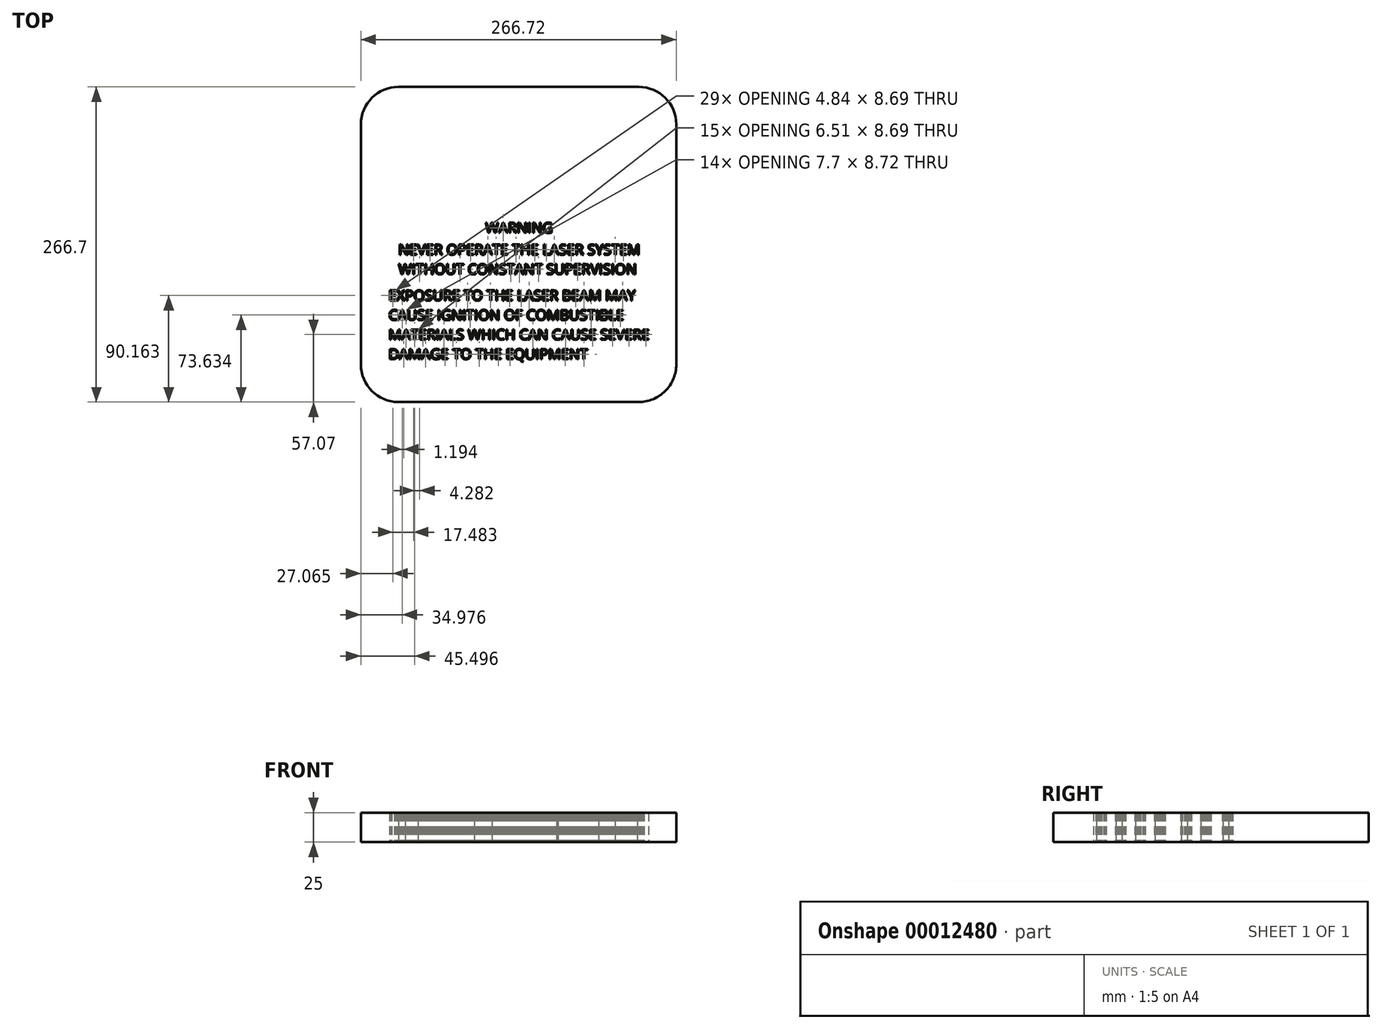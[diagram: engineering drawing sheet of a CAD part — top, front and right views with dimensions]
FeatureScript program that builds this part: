
annotation { "Feature Type Name" : "Feature", "Feature Type Description" : "" }
export const myFeature = defineFeature(function(context is Context, id is Id, definition is map)
    precondition{}
    {
        {
            var Q0;
            Q0=qCreatedBy(makeId("Top.planeOp"),FACE);
            var sketch = newSketch(context, id + "F0", { "sketchPlane" : qUnion([Q0])});
            skLineSegment(sketch, "E0.rect.top", {"start": v(101.61, 127) * mm, "end": v(-101.61, 127) * mm});
            skLineSegment(sketch, "E0.rect.left", {"start": v(127.01, -101.6) * mm, "end": v(127.01, 101.6) * mm});
            skLineSegment(sketch, "E0.rect.right", {"start": v(-127.01, -101.6) * mm, "end": v(-127.01, 101.6) * mm});
            skPoint(sketch, "E1.visualSharp", {"position": v(-127.01, 127) * mm});
            skArc(sketch, "E1.filletArc", {"start": v(-101.61, 127) * mm, "mid": v(-119.57, 119.56) * mm, "end": v(-127.01, 101.6) * mm});
            skPoint(sketch, "E2.visualSharp", {"position": v(127.01, 127) * mm});
            skArc(sketch, "E2.filletArc", {"start": v(127.01, 101.6) * mm, "mid": v(119.57, 119.56) * mm, "end": v(101.61, 127) * mm});
            skPoint(sketch, "E3.visualSharp", {"position": v(127.01, -127) * mm});
            skArc(sketch, "E3.filletArc", {"start": v(101.61, -127) * mm, "mid": v(119.57, -119.56) * mm, "end": v(127.01, -101.6) * mm});
            skPoint(sketch, "E4.visualSharp", {"position": v(-127.01, -127) * mm});
            skArc(sketch, "E4.filletArc", {"start": v(-127.01, -101.6) * mm, "mid": v(-119.57, -119.56) * mm, "end": v(-101.61, -127) * mm});
            skArc(sketch, "E5.0", {"start": v(-133.36, -101.6) * mm, "mid": v(-124.06, -124.05) * mm, "end": v(-101.61, -133.35) * mm});
            skLineSegment(sketch, "E5.1", {"start": v(101.6, -133.35) * mm, "end": v(-101.61, -133.35) * mm});
            skArc(sketch, "E5.2", {"start": v(101.6, -133.35) * mm, "mid": v(124.06, -124.06) * mm, "end": v(133.36, -101.6) * mm});
            skLineSegment(sketch, "E5.3", {"start": v(133.36, -101.6) * mm, "end": v(133.36, 101.6) * mm});
            skArc(sketch, "E5.4", {"start": v(133.36, 101.6) * mm, "mid": v(124.06, 124.05) * mm, "end": v(101.61, 133.35) * mm});
            skLineSegment(sketch, "E5.5", {"start": v(-133.36, -101.6) * mm, "end": v(-133.36, 101.6) * mm});
            skLineSegment(sketch, "E5.6", {"start": v(101.61, 133.35) * mm, "end": v(-101.61, 133.35) * mm});
            skArc(sketch, "E5.7", {"start": v(-101.61, 133.35) * mm, "mid": v(-124.06, 124.05) * mm, "end": v(-133.36, 101.6) * mm});
            skLineSegment(sketch, "E6", {"start": v(101.61, -127) * mm, "end": v(-101.61, -127) * mm});
            skText(sketch, "E7", { "text": "EXPOSURE TO THE LASER BEAM MAY\nCAUSE IGNITION OF COMBUSTIBLE\nMATERIALS WHICH CAN CAUSE SEVERE\nDAMAGE TO THE EQUIPMENT", "fontName": "OpenSans-Regular.ttf"});
            skText(sketch, "E8", { "text": "WARNING", "fontName": "OpenSans-Regular.ttf"});
            skText(sketch, "E9", { "text": "NEVER OPERATE THE LASER SYSTEM\nWITHOUT CONSTANT SUPERVISION", "fontName": "OpenSans-Regular.ttf"});
            skLineSegment(sketch, "E10.rect.bottom", {"start": v(113.7, -32.94) * mm, "end": v(-113.7, -32.94) * mm});
            skLineSegment(sketch, "E10.rect.top", {"start": v(113.7, -29.9) * mm, "end": v(-113.7, -29.9) * mm});
            skLineSegment(sketch, "E10.rect.left", {"start": v(113.7, -32.94) * mm, "end": v(113.7, -29.9) * mm});
            skLineSegment(sketch, "E10.rect.right", {"start": v(-113.7, -32.94) * mm, "end": v(-113.7, -29.9) * mm});
            skPoint(sketch, "E10.rect.middle", {"position": v(0, -31.42) * mm});
            skLineSegment(sketch, "E11", {"start": v(-37.8, 37.33) * mm, "end": v(37.68, 37.33) * mm});
            skLineSegment(sketch, "E12", {"start": v(-37.8, 37.33) * mm, "end": v(-0.06, 102.7) * mm});
            skLineSegment(sketch, "E13", {"start": v(-0.06, 102.7) * mm, "end": v(37.68, 37.33) * mm});
            skLineSegment(sketch, "E14.0", {"start": v(-0.06, 109.05) * mm, "end": v(43.18, 34.15) * mm});
            skLineSegment(sketch, "E14.1", {"start": v(-43.3, 34.15) * mm, "end": v(-0.06, 109.05) * mm});
            skLineSegment(sketch, "E14.2", {"start": v(-43.3, 34.15) * mm, "end": v(43.18, 34.15) * mm});
            skFitSpline(sketch, "E15", {"points": [v(-3.72, 39.82) * mm, v(-18.46, 40.85) * mm, v(-24.27, 54.87) * mm, v(-22.92, 51.92) * mm, v(-18.3, 46.98) * mm, v(-19.81, 50.89) * mm, v(-20.45, 61.56) * mm, v(-19.25, 57.74) * mm, v(-15.35, 53.35) * mm, v(-16.07, 55.74) * mm, v(-15.11, 71.35) * mm, v(-14.47, 68.33) * mm, v(-10.33, 61.48) * mm, v(-10.9, 63.7) * mm, v(-9.93, 80.43) * mm, v(-9.46, 77.57) * mm, v(-6.59, 70.16) * mm, v(-6.67, 72.95) * mm, v(1.53, 93.65) * mm, v(1.61, 88.87) * mm, v(6.87, 72.23) * mm, v(6.87, 73.82) * mm, v(9.18, 80.11) * mm, v(9.5, 77.17) * mm, v(12.13, 67.13) * mm, v(12.92, 69.68) * mm, v(14.51, 72.7) * mm, v(14.36, 69.84) * mm, v(19.7, 58.21) * mm, v(19.13, 56.78) * mm, v(22.08, 58.13) * mm, v(22.32, 60.44) * mm, v(23.83, 57.66) * mm, v(21.68, 43.8) * mm, v(2.8, 39.9) * mm, v(2.8, 39.9) * mm], "startDerivative": vector(-374.4, -97.5) * mm, "endDerivative": vector(15.91, -25.67) * mm});
            skFitSpline(sketch, "E16", {"points": [v(-3.72, 39.82) * mm, v(-9.85, 43.87) * mm, v(-11.9, 49.14) * mm, v(-10.53, 47.78) * mm, v(-6.97, 47.66) * mm, v(-8.16, 48.51) * mm, v(-8.38, 56.78) * mm, v(-6.9, 54.06) * mm, v(-4.98, 52.3) * mm, v(-4.3, 53.55) * mm, v(-1.98, 64.6) * mm, v(-1.76, 63.4) * mm, v(2.54, 56.55) * mm, v(2.88, 53.38) * mm, v(4.24, 53.9) * mm, v(7.3, 63.52) * mm, v(7.8, 62.38) * mm, v(8.83, 56.16) * mm, v(10.53, 54.34) * mm, v(14.32, 55.93) * mm, v(14.26, 54.8) * mm, v(13.58, 48.74) * mm, v(17.5, 48.12) * mm, v(17.26, 47.04) * mm, v(14.55, 44.21) * mm, v(2.8, 39.9) * mm], "startDerivative": vector(-126.1, 48) * mm, "endDerivative": vector(-194.69, -56.33) * mm});
            const initialGuessF0  = {"E7": [-0.10991, -0.04753, 1, 0, 0.00876], "E8": [-0.02808, 0.00973, 1, 0, 0.00876], "E9": [-0.1016, -0.00876, 1, 0, 0.00876]};
            skSetInitialGuess(sketch, initialGuessF0);
            skSolve(sketch);
        }
        {
            var Q0;
            Q0=makeQuery(id+"F0.imprint","IMPRINT",FACE,{"disambiguationData":[TD([[makeQuery(id+"F0.imprint","IMPRINT",EDGE,{"derivedFrom":sQuery(id+"F0.wireOp",EDGE,"E0.rect.top")}),-1.0]])]});
            var Q1;
            Q1=makeQuery(id+"F0.imprint","IMPRINT",FACE,{"disambiguationData":[TD([[makeQuery(id+"F0.imprint","IMPRINT",EDGE,{"derivedFrom":sQuery(id+"F0.wireOp",EDGE,"E0.rect.top")}),1.0]])]});
            var Q2;
            Q2=makeQuery(id+"F0.imprint","IMPRINT",FACE,{"disambiguationData":[TD([[makeQuery(id+"F0.imprint","IMPRINT",EDGE,{"derivedFrom":sQuery(id+"F0.wireOp",EDGE,"E11")}),-1.0]])]});
            var Q3;
            Q3=makeQuery(id+"F0.imprint","IMPRINT",FACE,{"disambiguationData":[TD([[makeQuery(id+"F0.imprint","IMPRINT",EDGE,{"derivedFrom":sQuery(id+"F0.wireOp",EDGE,"E11")}),1.0]])]});
            var Q4;
            Q4=makeQuery(id+"F0.imprint","IMPRINT",FACE,{"disambiguationData":[TD([[makeQuery(id+"F0.imprint","IMPRINT",EDGE,{"derivedFrom":sQuery(id+"F0.wireOp",EDGE,"E15")}),-1.0]])]});
            var Q5;
            Q5=makeQuery(id+"F0.imprint","IMPRINT",FACE,{"disambiguationData":[TD([[makeQuery(id+"F0.imprint","IMPRINT",EDGE,{"derivedFrom":sQuery(id+"F0.wireOp",EDGE,"E10.rect.bottom")}),-1.0]])]});
            extrude(context, id + "F1", {"entities" : qUnion([Q0, Q1, Q2, Q3, Q4, Q5]), "endBound" : BoundingType.SYMMETRIC, "depth" : 25 * mm});
        }
        {
            var Q0;
            Q0=makeQuery(id+"F0.imprint","IMPRINT",FACE,{"disambiguationData":[TD([[makeQuery(id+"F0.imprint","IMPRINT",EDGE,{"derivedFrom":sQuery(id+"F0.wireOp",EDGE,"E9.sketch_text.stroke-74")}),1.0]])]});
            var Q1;
            Q1=makeQuery(id+"F0.imprint","IMPRINT",FACE,{"disambiguationData":[TD([[makeQuery(id+"F0.imprint","IMPRINT",EDGE,{"derivedFrom":sQuery(id+"F0.wireOp",EDGE,"E9.sketch_text.stroke-90")}),1.0]])]});
            var Q2;
            Q2=makeQuery(id+"F0.imprint","IMPRINT",FACE,{"disambiguationData":[TD([[makeQuery(id+"F0.imprint","IMPRINT",EDGE,{"derivedFrom":sQuery(id+"F0.wireOp",EDGE,"E9.sketch_text.stroke-120")}),1.0]])]});
            var Q3;
            Q3=makeQuery(id+"F0.imprint","IMPRINT",FACE,{"disambiguationData":[TD([[makeQuery(id+"F0.imprint","IMPRINT",EDGE,{"derivedFrom":sQuery(id+"F0.wireOp",EDGE,"E9.sketch_text.stroke-59")}),1.0]])]});
            var Q4;
            Q4=makeQuery(id+"F0.imprint","IMPRINT",FACE,{"disambiguationData":[TD([[makeQuery(id+"F0.imprint","IMPRINT",EDGE,{"derivedFrom":sQuery(id+"F0.wireOp",EDGE,"E9.sketch_text.stroke-135")}),1.0]])]});
            var Q5;
            Q5=makeQuery(id+"F0.imprint","IMPRINT",FACE,{"disambiguationData":[TD([[makeQuery(id+"F0.imprint","IMPRINT",EDGE,{"derivedFrom":sQuery(id+"F0.wireOp",EDGE,"E9.sketch_text.stroke-206")}),1.0]])]});
            var Q6;
            Q6=makeQuery(id+"F0.imprint","IMPRINT",FACE,{"disambiguationData":[TD([[makeQuery(id+"F0.imprint","IMPRINT",EDGE,{"derivedFrom":sQuery(id+"F0.wireOp",EDGE,"E8.sketch_text.stroke-44")}),1.0]])]});
            var Q7;
            Q7=makeQuery(id+"F0.imprint","IMPRINT",FACE,{"disambiguationData":[TD([[makeQuery(id+"F0.imprint","IMPRINT",EDGE,{"derivedFrom":sQuery(id+"F0.wireOp",EDGE,"E8.sketch_text.stroke-28")}),1.0]])]});
            var Q8;
            Q8=makeQuery(id+"F0.imprint","IMPRINT",FACE,{"disambiguationData":[TD([[makeQuery(id+"F0.imprint","IMPRINT",EDGE,{"derivedFrom":sQuery(id+"F0.wireOp",EDGE,"E9.sketch_text.stroke-259")}),1.0]])]});
            var Q9;
            Q9=makeQuery(id+"F0.imprint","IMPRINT",FACE,{"disambiguationData":[TD([[makeQuery(id+"F0.imprint","IMPRINT",EDGE,{"derivedFrom":sQuery(id+"F0.wireOp",EDGE,"E9.sketch_text.stroke-694")}),1.0]])]});
            var Q10;
            Q10=makeQuery(id+"F0.imprint","IMPRINT",FACE,{"disambiguationData":[TD([[makeQuery(id+"F0.imprint","IMPRINT",EDGE,{"derivedFrom":sQuery(id+"F0.wireOp",EDGE,"E9.sketch_text.stroke-637")}),1.0]])]});
            var Q11;
            Q11=makeQuery(id+"F0.imprint","IMPRINT",FACE,{"disambiguationData":[TD([[makeQuery(id+"F0.imprint","IMPRINT",EDGE,{"derivedFrom":sQuery(id+"F0.wireOp",EDGE,"E9.sketch_text.stroke-607")}),1.0]])]});
            var Q12;
            Q12=makeQuery(id+"F0.imprint","IMPRINT",FACE,{"disambiguationData":[TD([[makeQuery(id+"F0.imprint","IMPRINT",EDGE,{"derivedFrom":sQuery(id+"F0.wireOp",EDGE,"E9.sketch_text.stroke-532")}),1.0]])]});
            var Q13;
            Q13=makeQuery(id+"F0.imprint","IMPRINT",FACE,{"disambiguationData":[TD([[makeQuery(id+"F0.imprint","IMPRINT",EDGE,{"derivedFrom":sQuery(id+"F0.wireOp",EDGE,"E9.sketch_text.stroke-468")}),1.0]])]});
            var Q14;
            Q14=makeQuery(id+"F0.imprint","IMPRINT",FACE,{"disambiguationData":[TD([[makeQuery(id+"F0.imprint","IMPRINT",EDGE,{"derivedFrom":sQuery(id+"F0.wireOp",EDGE,"E9.sketch_text.stroke-415")}),1.0]])]});
            var Q15;
            Q15=makeQuery(id+"F0.imprint","IMPRINT",FACE,{"disambiguationData":[TD([[makeQuery(id+"F0.imprint","IMPRINT",EDGE,{"derivedFrom":sQuery(id+"F0.wireOp",EDGE,"E7.sketch_text.stroke-47")}),1.0]])]});
            var Q16;
            Q16=makeQuery(id+"F0.imprint","IMPRINT",FACE,{"disambiguationData":[TD([[makeQuery(id+"F0.imprint","IMPRINT",EDGE,{"derivedFrom":sQuery(id+"F0.wireOp",EDGE,"E7.sketch_text.stroke-32")}),1.0]])]});
            var Q17;
            Q17=makeQuery(id+"F0.imprint","IMPRINT",FACE,{"disambiguationData":[TD([[makeQuery(id+"F0.imprint","IMPRINT",EDGE,{"derivedFrom":sQuery(id+"F0.wireOp",EDGE,"E7.sketch_text.stroke-105")}),1.0]])]});
            var Q18;
            Q18=makeQuery(id+"F0.imprint","IMPRINT",FACE,{"disambiguationData":[TD([[makeQuery(id+"F0.imprint","IMPRINT",EDGE,{"derivedFrom":sQuery(id+"F0.wireOp",EDGE,"E7.sketch_text.stroke-140")}),1.0]])]});
            var Q19;
            Q19=makeQuery(id+"F0.imprint","IMPRINT",FACE,{"disambiguationData":[TD([[makeQuery(id+"F0.imprint","IMPRINT",EDGE,{"derivedFrom":sQuery(id+"F0.wireOp",EDGE,"E7.sketch_text.stroke-194")}),1.0]])]});
            var Q20;
            Q20=makeQuery(id+"F0.imprint","IMPRINT",FACE,{"disambiguationData":[TD([[makeQuery(id+"F0.imprint","IMPRINT",EDGE,{"derivedFrom":sQuery(id+"F0.wireOp",EDGE,"E7.sketch_text.stroke-247")}),1.0]])]});
            var Q21;
            Q21=makeQuery(id+"F0.imprint","IMPRINT",FACE,{"disambiguationData":[TD([[makeQuery(id+"F0.imprint","IMPRINT",EDGE,{"derivedFrom":sQuery(id+"F0.wireOp",EDGE,"E7.sketch_text.stroke-272")}),1.0]])]});
            var Q22;
            Q22=makeQuery(id+"F0.imprint","IMPRINT",FACE,{"disambiguationData":[TD([[makeQuery(id+"F0.imprint","IMPRINT",EDGE,{"derivedFrom":sQuery(id+"F0.wireOp",EDGE,"E7.sketch_text.stroke-265")}),1.0]])]});
            var Q23;
            Q23=makeQuery(id+"F0.imprint","IMPRINT",FACE,{"disambiguationData":[TD([[makeQuery(id+"F0.imprint","IMPRINT",EDGE,{"derivedFrom":sQuery(id+"F0.wireOp",EDGE,"E7.sketch_text.stroke-299")}),1.0]])]});
            var Q24;
            Q24=makeQuery(id+"F0.imprint","IMPRINT",FACE,{"disambiguationData":[TD([[makeQuery(id+"F0.imprint","IMPRINT",EDGE,{"derivedFrom":sQuery(id+"F0.wireOp",EDGE,"E7.sketch_text.stroke-348")}),1.0]])]});
            var Q25;
            Q25=makeQuery(id+"F0.imprint","IMPRINT",FACE,{"disambiguationData":[TD([[makeQuery(id+"F0.imprint","IMPRINT",EDGE,{"derivedFrom":sQuery(id+"F0.wireOp",EDGE,"E7.sketch_text.stroke-696")}),1.0]])]});
            var Q26;
            Q26=makeQuery(id+"F0.imprint","IMPRINT",FACE,{"disambiguationData":[TD([[makeQuery(id+"F0.imprint","IMPRINT",EDGE,{"derivedFrom":sQuery(id+"F0.wireOp",EDGE,"E7.sketch_text.stroke-689")}),1.0]])]});
            var Q27;
            Q27=makeQuery(id+"F0.imprint","IMPRINT",FACE,{"disambiguationData":[TD([[makeQuery(id+"F0.imprint","IMPRINT",EDGE,{"derivedFrom":sQuery(id+"F0.wireOp",EDGE,"E7.sketch_text.stroke-620")}),1.0]])]});
            var Q28;
            Q28=makeQuery(id+"F0.imprint","IMPRINT",FACE,{"disambiguationData":[TD([[makeQuery(id+"F0.imprint","IMPRINT",EDGE,{"derivedFrom":sQuery(id+"F0.wireOp",EDGE,"E7.sketch_text.stroke-613")}),1.0]])]});
            var Q29;
            Q29=makeQuery(id+"F0.imprint","IMPRINT",FACE,{"disambiguationData":[TD([[makeQuery(id+"F0.imprint","IMPRINT",EDGE,{"derivedFrom":sQuery(id+"F0.wireOp",EDGE,"E7.sketch_text.stroke-535")}),1.0]])]});
            var Q30;
            Q30=makeQuery(id+"F0.imprint","IMPRINT",FACE,{"disambiguationData":[TD([[makeQuery(id+"F0.imprint","IMPRINT",EDGE,{"derivedFrom":sQuery(id+"F0.wireOp",EDGE,"E7.sketch_text.stroke-385")}),1.0]])]});
            var Q31;
            Q31=makeQuery(id+"F0.imprint","IMPRINT",FACE,{"disambiguationData":[TD([[makeQuery(id+"F0.imprint","IMPRINT",EDGE,{"derivedFrom":sQuery(id+"F0.wireOp",EDGE,"E7.sketch_text.stroke-1092")}),1.0]])]});
            var Q32;
            Q32=makeQuery(id+"F0.imprint","IMPRINT",FACE,{"disambiguationData":[TD([[makeQuery(id+"F0.imprint","IMPRINT",EDGE,{"derivedFrom":sQuery(id+"F0.wireOp",EDGE,"E7.sketch_text.stroke-967")}),1.0]])]});
            var Q33;
            Q33=makeQuery(id+"F0.imprint","IMPRINT",FACE,{"disambiguationData":[TD([[makeQuery(id+"F0.imprint","IMPRINT",EDGE,{"derivedFrom":sQuery(id+"F0.wireOp",EDGE,"E7.sketch_text.stroke-924")}),1.0]])]});
            var Q34;
            Q34=makeQuery(id+"F0.imprint","IMPRINT",FACE,{"disambiguationData":[TD([[makeQuery(id+"F0.imprint","IMPRINT",EDGE,{"derivedFrom":sQuery(id+"F0.wireOp",EDGE,"E7.sketch_text.stroke-576")}),1.0]])]});
            var Q35;
            Q35=makeQuery(id+"F0.imprint","IMPRINT",FACE,{"disambiguationData":[TD([[makeQuery(id+"F0.imprint","IMPRINT",EDGE,{"derivedFrom":sQuery(id+"F0.wireOp",EDGE,"E7.sketch_text.stroke-504")}),1.0]])]});
            var Q36;
            Q36=makeQuery(id+"F0.imprint","IMPRINT",FACE,{"disambiguationData":[TD([[makeQuery(id+"F0.imprint","IMPRINT",EDGE,{"derivedFrom":sQuery(id+"F0.wireOp",EDGE,"E7.sketch_text.stroke-747")}),1.0]])]});
            var Q37;
            Q37=makeQuery(id+"F0.imprint","IMPRINT",FACE,{"disambiguationData":[TD([[makeQuery(id+"F0.imprint","IMPRINT",EDGE,{"derivedFrom":sQuery(id+"F0.wireOp",EDGE,"E7.sketch_text.stroke-783")}),1.0]])]});
            var Q38;
            Q38=makeQuery(id+"F0.imprint","IMPRINT",FACE,{"disambiguationData":[TD([[makeQuery(id+"F0.imprint","IMPRINT",EDGE,{"derivedFrom":sQuery(id+"F0.wireOp",EDGE,"E7.sketch_text.stroke-802")}),1.0]])]});
            var Q39;
            Q39=makeQuery(id+"F0.imprint","IMPRINT",FACE,{"disambiguationData":[TD([[makeQuery(id+"F0.imprint","IMPRINT",EDGE,{"derivedFrom":sQuery(id+"F0.wireOp",EDGE,"E7.sketch_text.stroke-1315")}),1.0]])]});
            var Q40;
            Q40=makeQuery(id+"F0.imprint","IMPRINT",FACE,{"disambiguationData":[TD([[makeQuery(id+"F0.imprint","IMPRINT",EDGE,{"derivedFrom":sQuery(id+"F0.wireOp",EDGE,"E7.sketch_text.stroke-1281")}),1.0]])]});
            var Q41;
            Q41=makeQuery(id+"F0.imprint","IMPRINT",FACE,{"disambiguationData":[TD([[makeQuery(id+"F0.imprint","IMPRINT",EDGE,{"derivedFrom":sQuery(id+"F0.wireOp",EDGE,"E7.sketch_text.stroke-1217")}),1.0]])]});
            var Q42;
            Q42=makeQuery(id+"F0.imprint","IMPRINT",FACE,{"disambiguationData":[TD([[makeQuery(id+"F0.imprint","IMPRINT",EDGE,{"derivedFrom":sQuery(id+"F0.wireOp",EDGE,"E7.sketch_text.stroke-1164")}),1.0]])]});
            var Q43;
            Q43=makeQuery(id+"F0.imprint","IMPRINT",FACE,{"disambiguationData":[TD([[makeQuery(id+"F0.imprint","IMPRINT",EDGE,{"derivedFrom":sQuery(id+"F0.wireOp",EDGE,"E7.sketch_text.stroke-1133")}),1.0]])]});
            var Q44;
            Q44=makeQuery(id+"F0.imprint","IMPRINT",FACE,{"disambiguationData":[TD([[makeQuery(id+"F0.imprint","IMPRINT",EDGE,{"derivedFrom":sQuery(id+"F0.wireOp",EDGE,"E7.sketch_text.stroke-1118")}),1.0]])]});
            extrude(context, id + "F2", {"entities" : qUnion([Q0, Q1, Q2, Q3, Q4, Q5, Q6, Q7, Q8, Q9, Q10, Q11, Q12, Q13, Q14, Q15, Q16, Q17, Q18, Q19, Q20, Q21, Q22, Q23, Q24, Q25, Q26, Q27, Q28, Q29, Q30, Q31, Q32, Q33, Q34, Q35, Q36, Q37, Q38, Q39, Q40, Q41, Q42, Q43, Q44]), "endBound" : BoundingType.SYMMETRIC, "depth" : 25 * mm});
        }
    });
